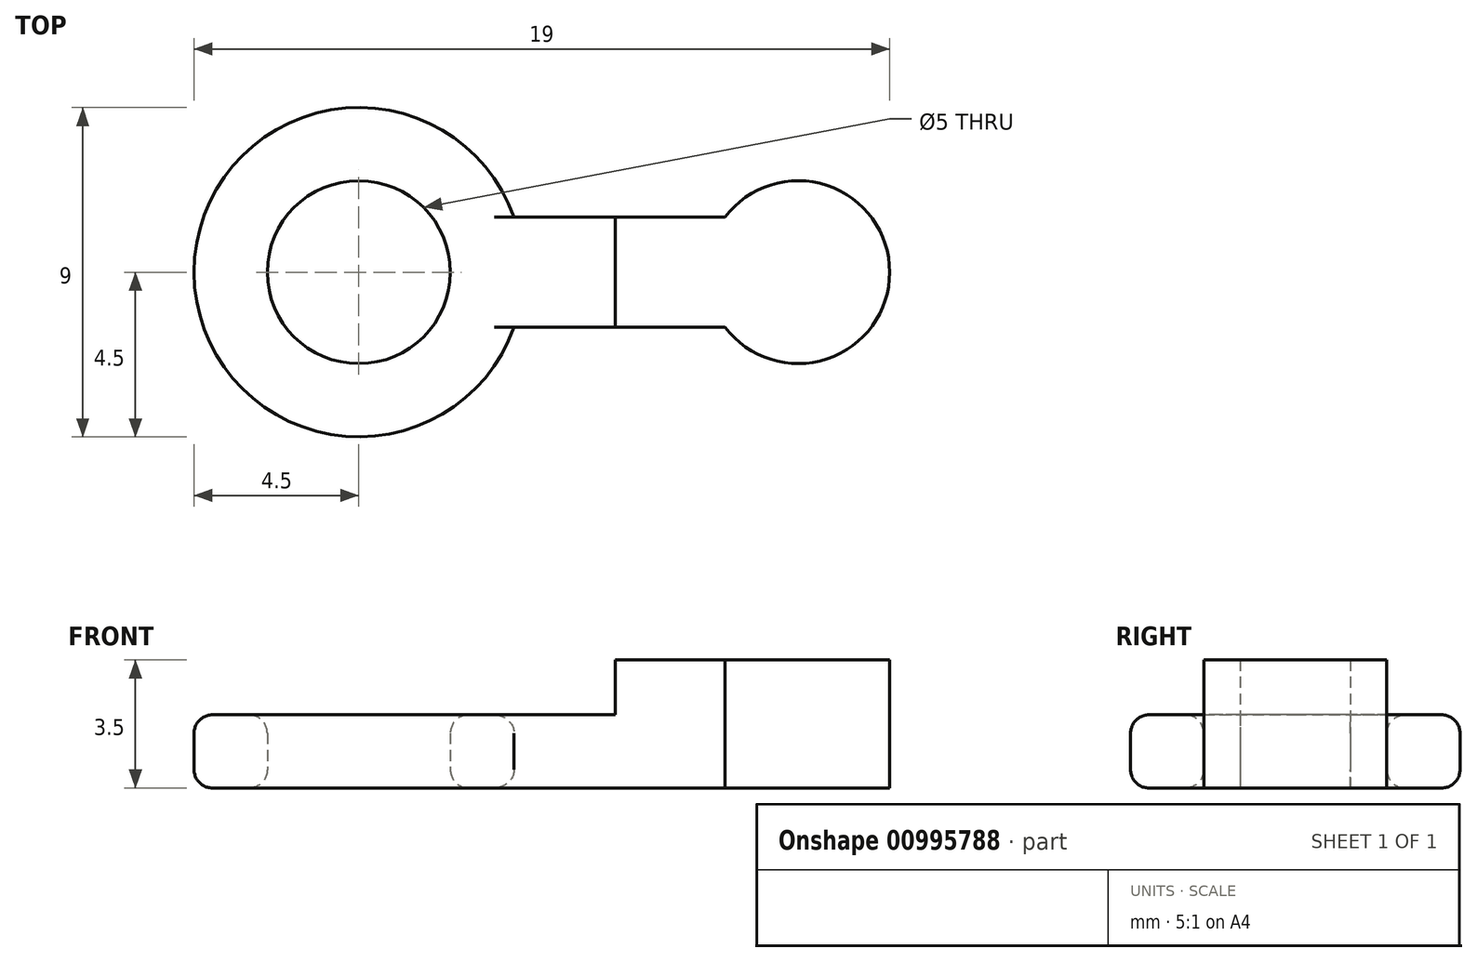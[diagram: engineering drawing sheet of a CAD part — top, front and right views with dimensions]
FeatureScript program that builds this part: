
annotation { "Feature Type Name" : "Feature", "Feature Type Description" : "" }
export const myFeature = defineFeature(function(context is Context, id is Id, definition is map)
    precondition{}
    {
        {
            var Q0;
            Q0=qCreatedBy(makeId("Top.planeOp"),FACE);
            var sketch = newSketch(context, id + "F0", { "sketchPlane" : qUnion([Q0])});
            skCircle(sketch, "E0", {"center": v(0, 0) * mm, "radius": 2.5 * mm});
            skCircle(sketch, "E1", {"center": v(0, 0) * mm, "radius": 4.5 * mm});
            skCircle(sketch, "E2", {"center": v(12, 0) * mm, "radius": 2.5 * mm});
            skLineSegment(sketch, "E3", {"start": v(4.24, 1.5) * mm, "end": v(10, 1.5) * mm});
            skLineSegment(sketch, "E4.MirrorCS", {"start": v(4.24, -1.5) * mm, "end": v(10, -1.5) * mm});
            skSolve(sketch);
        }
        {
            var Q0;
            Q0=makeQuery(id+"F0.imprint","IMPRINT",FACE,{"disambiguationData":[TD([[makeQuery(id+"F0.imprint","IMPRINT",EDGE,{"derivedFrom":sQuery(id+"F0.wireOp",EDGE,"E0")}),-1.0]])]});
            var Q1;
            {var subQ0=sQuery(id+"F0.wireOp",EDGE,"E3");Q1=makeQuery(id+"F0.imprint","IMPRINT",FACE,{"disambiguationData":[TD([[makeQuery(id+"F0.imprint","IMPRINT",EDGE,{"derivedFrom":subQ0}),-1.0]])]});}
            var Q2;
            {var subQ0=sQuery(id+"F0.wireOp",EDGE,"E2");var subQ1=makeQuery(id+"F0.imprint","INTERSECT",VERTEX,{"derivedFrom":[subQ0,sQuery(id+"F0.wireOp",EDGE,"E3")]});Q2=makeQuery(id+"F0.imprint","IMPRINT",FACE,{"disambiguationData":[TD([[makeQuery(id+"F0.imprint","IMPRINT",EDGE,{"disambiguationData":[TD([[subQ1,-1.0]])],"derivedFrom":subQ0}),1.0]])]});}
            extrude(context, id + "F1", {"entities" : qUnion([Q0, Q1, Q2]), "depth" : 2 * mm, "offsetDistance" : 25 * mm});
        }
        {
            var Q0;
            Q0=makeQuery(id+"F1.opExtrude","CAP_FACE",FACE,{"disambiguationData":[OSD([sQuery(id+"F0.wireOp",EDGE,"E0"),sQuery(id+"F0.wireOp",EDGE,"E1"),sQuery(id+"F0.wireOp",EDGE,"E2"),sQuery(id+"F0.wireOp",EDGE,"E3"),sQuery(id+"F0.wireOp",EDGE,"E4.MirrorCS")])],"isStart":false});
            var sketch = newSketch(context, id + "F2", { "sketchPlane" : qUnion([Q0])});
            skCircle(sketch, "E5", {"center": v(12, 0) * mm, "radius": 2.5 * mm});
            skLineSegment(sketch, "E6", {"start": v(7, 1.5) * mm, "end": v(7, -1.5) * mm});
            skLineSegment(sketch, "E7", {"start": v(7, 1.5) * mm, "end": v(10, 1.5) * mm});
            skLineSegment(sketch, "E8", {"start": v(12, 0) * mm, "end": v(-4.01, 0) * mm, "construction": true});
            skLineSegment(sketch, "E9.MirrorCS", {"start": v(7, -1.5) * mm, "end": v(10, -1.5) * mm});
            skSolve(sketch);
        }
        {
            var Q0;
            {var subQ0=sQuery(id+"F2.wireOp",EDGE,"E5");var subQ1=makeQuery(id+"F2.imprint","INTERSECT",VERTEX,{"derivedFrom":[makeQuery(id+"F1.opExtrude","CAP_EDGE",EDGE,{"disambiguationData":[OSD([sQuery(id+"F0.wireOp",EDGE,"E3")])],"isStart":false}),subQ0]});Q0=makeQuery(id+"F2.imprint","IMPRINT",FACE,{"disambiguationData":[TD([[makeQuery(id+"F2.imprint","IMPRINT",EDGE,{"disambiguationData":[TD([[subQ1,-1.0]])],"derivedFrom":subQ0}),1.0]])]});}
            var Q1;
            Q1=makeQuery(id+"F2.imprint","IMPRINT",FACE,{"disambiguationData":[TD([[makeQuery(id+"F2.imprint","IMPRINT",EDGE,{"derivedFrom":sQuery(id+"F2.wireOp",EDGE,"E6")}),1.0]])]});
            extrude(context, id + "F3", {"entities" : qUnion([Q0, Q1]), "operationType" : NewBodyOperationType.ADD, "depth" : 1.5 * mm, "offsetDistance" : 25 * mm});
        }
        {
            var Q0;
            Q0=makeQuery(id+"F1.opExtrude","CAP_EDGE",EDGE,{"disambiguationData":[OSD([sQuery(id+"F0.wireOp",EDGE,"E0")])],"isStart":false});
            var Q1;
            Q1=makeQuery(id+"F1.opExtrude","CAP_EDGE",EDGE,{"disambiguationData":[OSD([sQuery(id+"F0.wireOp",EDGE,"E1")])],"isStart":false});
            var Q2;
            Q2=makeQuery(id+"F1.opExtrude","CAP_EDGE",EDGE,{"disambiguationData":[OSD([sQuery(id+"F0.wireOp",EDGE,"E1")])],"isStart":true});
            var Q3;
            Q3=makeQuery(id+"F1.opExtrude","CAP_EDGE",EDGE,{"disambiguationData":[OSD([sQuery(id+"F0.wireOp",EDGE,"E0")])],"isStart":true});
            fillet(context, id + "F4", {"entities" : qUnion([Q0, Q1, Q2, Q3]), "radius" : .5 * mm, "tangentPropagation" : true, "allowEdgeOverflow" : false});
        }
    });
